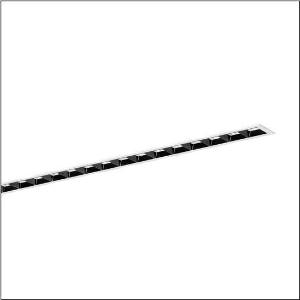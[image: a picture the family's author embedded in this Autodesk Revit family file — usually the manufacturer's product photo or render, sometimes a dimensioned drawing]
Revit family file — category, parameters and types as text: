
# Revit family: silica_r__21_51mx11dc4awb_441a
name_source: partatom
category: Lighting Fixtures
units: mm (PartAtom-declared; Revit-internal decimal feet)

## family parameters
Cut with Voids When Loaded = No
Host = Face
Light Source = No
Part Type = Normal
Room Calculation Point = No
Round Connector Dimension = Use Diameter
Shared = No

## types (1)
- --- (1 x LED, 10800 lm, 64.8 W, 4000K)
    Apparent Load = 65 VA
    CIE Flux Codes = 87 99 100 100 100
    Color Rendering = 80
    Color Temperature = 4000K
    Default Elevation = 1800 mm
    Description = Silica® 21, office luminaire, primary light control with darklight reflector, of PMMA, black, CAT 2 (L<= 3000cd/m²), light emission: direct distribution, primary light characteristic: symmetric, installation type: recessed, LED, rated luminous flux: 10.800lm, luminous efficacy: 167lm/W, light colour: 840, colour temperature: 4000K, with terminal, 3+2-pole, max. 2.5mm², mains connection: 220..240V, AC, 50/60Hz, rated input power: 64.8W, luminaire housing, of aluminium, traffic white (RAL 9016), length: 3.028mm, width: 79mm, height: 53mm, protection rating (complete): IP20, insulation class (complete): insulation class I (protective earthing), certification: CE, permissible operating ambient temperature: 0..+35°C, standard: EN 50419, packaging unit: 1 piece
    Height = 0 mm  [stored 0 ft]
    Lamp = 1 x LED
    Lamp Light Flux = 10800 lm
    Lamp Power = 64.8 W
    Lamp count = 1
    Length = 3027 mm
    Luminous efficacy = 167 lm/W
    Manufacturer = Siteco
    ModVariant = No
    Model = 51MX11DC4AWB
    Mounting Place = Ceiling
    Mounting Type = Recessed
    Number of Poles = 1
    OnlyDefault = Yes
    Power Factor = 1
    Product Name = Silica® 21
    Product group = office luminaire | ceiling recessed
    ProductGroupID = 401
    Protection Class = Protection class I
    Protection Degree = IP 20
    RLX_Detail_Level = 1
    RLX_Emergency_Light_Flux = 0 lm
    RLX_Emergency_Type = 0
    RLX_Emergency_Type_DB = No
    RlxData = <blob elided: 62553 chars, md5=31c5dca9>
    Socket = socket
    Standby Power = 0 W
    System Light Flux = 10800 lm
    System Power = 65 W
    Type Comments = factory setting: luminous flux: 100 % | dim-lin: 254 | 367 mA
    Type Image = l_1297791.jpg
    URL = http://relux.com
    VarID = @adj_054065
    Voltage = 0 V
    Weight = 0.00 kg
    Width = 79 mm

note: [stored X ft] marks values corroborated as IEEE doubles in the binary element streams (Revit-internal decimal feet)

## geometry (parser evidence)
native form markers: Blend x4, Sweep x11
no freeform markers — native parametric forms only
